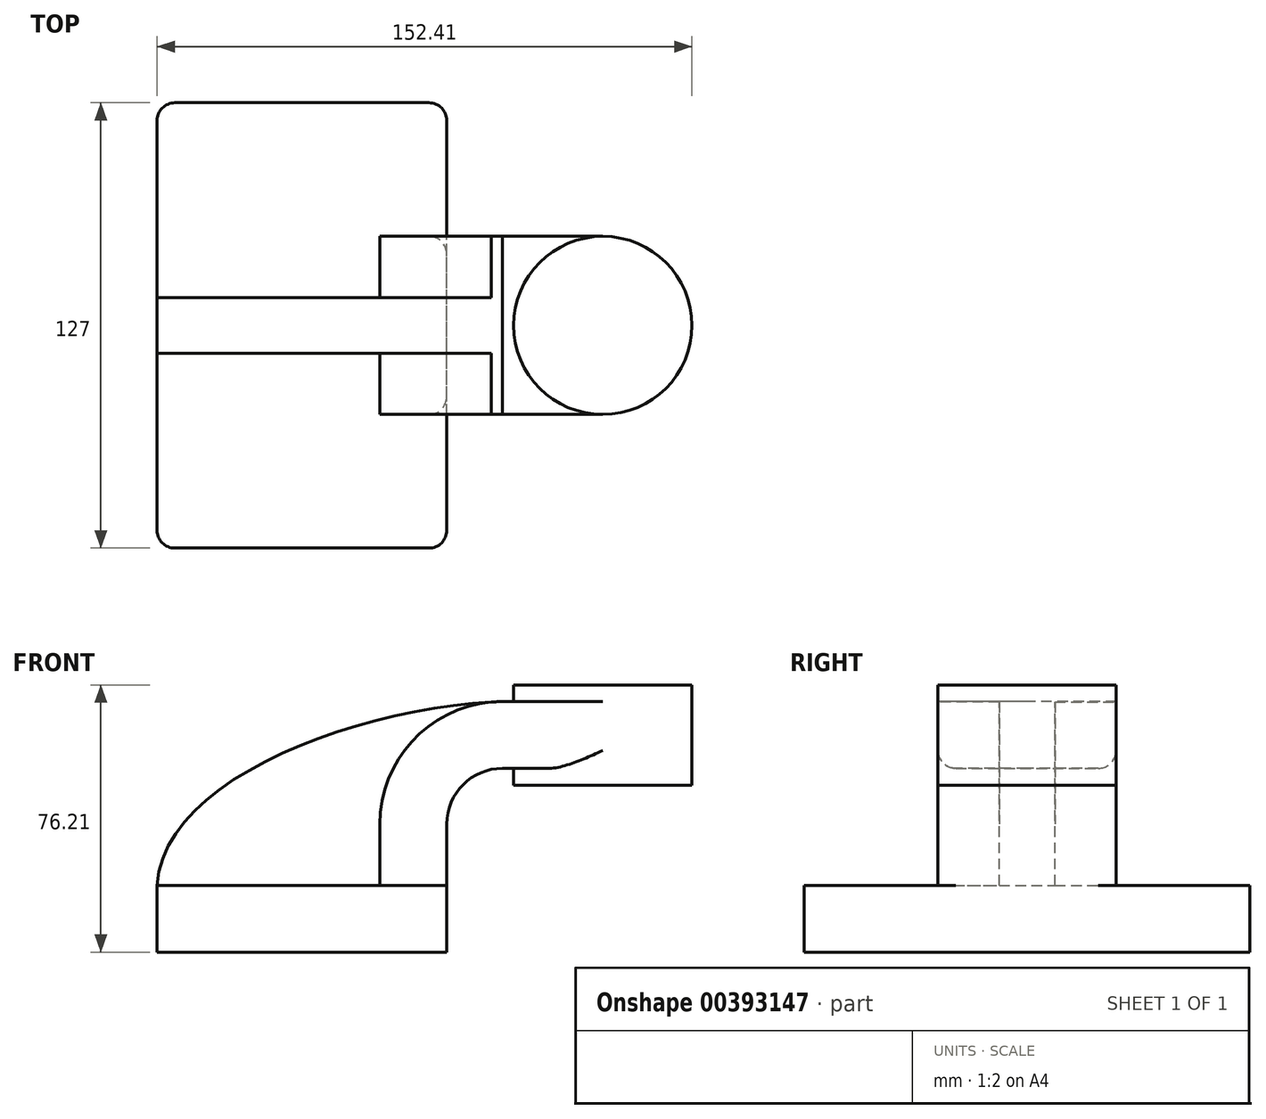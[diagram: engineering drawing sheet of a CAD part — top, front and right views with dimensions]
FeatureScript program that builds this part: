
annotation { "Feature Type Name" : "Feature", "Feature Type Description" : "" }
export const myFeature = defineFeature(function(context is Context, id is Id, definition is map)
    precondition{}
    {
        {
            var Q0;
            Q0=qCreatedBy(makeId("Front.planeOp"),FACE);
            var sketch = newSketch(context, id + "F0", { "sketchPlane" : qUnion([Q0])});
            skLineSegment(sketch, "E0.rect.bottom", {"start": v(-41.28, 9.52) * mm, "end": v(41.28, 9.52) * mm});
            skLineSegment(sketch, "E0.rect.top", {"start": v(-41.28, -9.52) * mm, "end": v(41.28, -9.52) * mm});
            skLineSegment(sketch, "E0.rect.left", {"start": v(-41.28, 9.52) * mm, "end": v(-41.28, -9.52) * mm});
            skLineSegment(sketch, "E0.rect.right", {"start": v(41.28, 9.52) * mm, "end": v(41.28, -9.52) * mm});
            skPoint(sketch, "E0.rect.middle", {"position": v(0, 0) * mm});
            skLineSegment(sketch, "E1", {"start": v(41.28, 9.52) * mm, "end": v(41.28, 27) * mm});
            skArc(sketch, "E2", {"start": v(41.28, 27) * mm, "mid": v(45.92, 38.23) * mm, "end": v(57.15, 42.88) * mm});
            skLineSegment(sketch, "E3", {"start": v(57.15, 42.88) * mm, "end": v(85.72, 42.88) * mm});
            skLineSegment(sketch, "E4.rect.bottom", {"start": v(60.32, 38.1) * mm, "end": v(111.12, 38.1) * mm});
            skLineSegment(sketch, "E4.rect.top", {"start": v(60.32, 66.68) * mm, "end": v(111.12, 66.68) * mm});
            skLineSegment(sketch, "E4.rect.left", {"start": v(60.32, 38.1) * mm, "end": v(60.32, 66.68) * mm});
            skLineSegment(sketch, "E4.rect.right", {"start": v(111.13, 38.1) * mm, "end": v(111.12, 66.68) * mm});
            skPoint(sketch, "E4.rect.middle", {"position": v(85.72, 52.39) * mm});
            skLineSegment(sketch, "E5.0", {"start": v(57.15, 61.93) * mm, "end": v(85.72, 61.93) * mm});
            skArc(sketch, "E5.1", {"start": v(22.23, 27) * mm, "mid": v(32.45, 51.7) * mm, "end": v(57.15, 61.93) * mm});
            skLineSegment(sketch, "E5.2", {"start": v(22.23, 9.52) * mm, "end": v(22.23, 27) * mm});
            skLineSegment(sketch, "E6", {"start": v(85.72, 38.1) * mm, "end": v(85.72, 66.68) * mm});
            skFitSpline(sketch, "E7", {"points": [v(-41.28, 9.53) * mm, v(57.15, 61.93) * mm], "startDerivative": vector(5.2, 92.34) * mm, "endDerivative": vector(120.92, 4.22) * mm});
            skSolve(sketch);
        }
        {
            var Q0;
            {var subQ4=sQuery(id+"F0.wireOp",EDGE,"E1");Q0=makeQuery(id+"F0.imprint","IMPRINT",FACE,{"disambiguationData":[TD([[makeQuery(id+"F0.imprint","IMPRINT",EDGE,{"derivedFrom":subQ4}),1.0]])]});}
            var Q1;
            {var subQ0=sQuery(id+"F0.wireOp",EDGE,"E6");var subQ1=sQuery(id+"F0.wireOp",EDGE,"E3");var subQ2=makeQuery(id+"F0.imprint","INTERSECT",VERTEX,{"derivedFrom":[subQ1,subQ0]});Q1=makeQuery(id+"F0.imprint","IMPRINT",FACE,{"disambiguationData":[TD([[makeQuery(id+"F0.imprint","IMPRINT",EDGE,{"disambiguationData":[TD([[subQ2,1.0]])],"derivedFrom":subQ1}),1.0]])]});}
            extrude(context, id + "F1", {"entities" : qUnion([Q0, Q1]), "endBound" : BoundingType.SYMMETRIC, "depth" : 12.7 * mm});
        }
        {
            var Q0;
            {var subQ0=sQuery(id+"F0.wireOp",EDGE,"E4.rect.right");Q0=makeQuery(id+"F0.imprint","IMPRINT",FACE,{"disambiguationData":[TD([[makeQuery(id+"F0.imprint","IMPRINT",EDGE,{"derivedFrom":subQ0}),1.0]])]});}
            var Q1;
            Q1=sQuery(id+"F0.wireOp",EDGE,"E6");
            revolve(context, id + "F2", {"operationType" : NewBodyOperationType.ADD, "entities" : qUnion([Q0]), "axis" : qUnion([Q1]), "revolveType" : RevolveType.FULL});
        }
        {
            var Q0;
            Q0=makeQuery(id+"F0.imprint","IMPRINT",FACE,{"disambiguationData":[TD([[makeQuery(id+"F0.imprint","IMPRINT",EDGE,{"derivedFrom":sQuery(id+"F0.wireOp",EDGE,"E0.rect.top")}),1.0]])]});
            extrude(context, id + "F3", {"entities" : qUnion([Q0]), "endBound" : BoundingType.SYMMETRIC, "depth" : 127 * mm});
        }
        {
            var Q0;
            {var subQ9=sQuery(id+"F0.wireOp",EDGE,"E1");Q0=makeQuery(id+"F0.imprint","IMPRINT",FACE,{"disambiguationData":[TD([[makeQuery(id+"F0.imprint","IMPRINT",EDGE,{"derivedFrom":subQ9}),1.0]])]});}
            var Q1;
            {var subQ0=sQuery(id+"F0.wireOp",EDGE,"E6");var subQ1=sQuery(id+"F0.wireOp",EDGE,"E3");var subQ2=makeQuery(id+"F0.imprint","INTERSECT",VERTEX,{"derivedFrom":[subQ1,subQ0]});Q1=makeQuery(id+"F0.imprint","IMPRINT",FACE,{"disambiguationData":[TD([[makeQuery(id+"F0.imprint","IMPRINT",EDGE,{"disambiguationData":[TD([[subQ2,1.0]])],"derivedFrom":subQ1}),1.0]])]});}
            extrude(context, id + "F4", {"entities" : qUnion([Q0, Q1]), "operationType" : NewBodyOperationType.ADD, "endBound" : BoundingType.SYMMETRIC, "depth" : 50.8 * mm});
        }
        {
            var Q0;
            {var subQ3=sQuery(id+"F0.wireOp",EDGE,"E5.2");Q0=makeQuery(id+"F0.imprint","IMPRINT",FACE,{"disambiguationData":[TD([[makeQuery(id+"F0.imprint","IMPRINT",EDGE,{"derivedFrom":subQ3}),1.0]])]});}
            extrude(context, id + "F5", {"entities" : qUnion([Q0]), "operationType" : NewBodyOperationType.ADD, "endBound" : BoundingType.SYMMETRIC, "depth" : 15.88 * mm});
        }
        {
            var Q0;
            {var subQ5=sQuery(id+"F0.wireOp",EDGE,"E4.rect.right");Q0=makeQuery(id+"F0.imprint","IMPRINT",FACE,{"disambiguationData":[TD([[makeQuery(id+"F0.imprint","IMPRINT",EDGE,{"derivedFrom":subQ5}),1.0]])]});}
            var Q1;
            Q1=sQuery(id+"F0.wireOp",EDGE,"E6");
            revolve(context, id + "F6", {"operationType" : NewBodyOperationType.ADD, "entities" : qUnion([Q0]), "axis" : qUnion([Q1]), "revolveType" : RevolveType.FULL});
        }
        {
            var Q0;
            Q0=makeQuery(id+"F3.opExtrude","CAP_EDGE",EDGE,{"disambiguationData":[OSD([sQuery(id+"F0.wireOp",EDGE,"E0.rect.right")])],"isStart":false});
            var Q1;
            Q1=makeQuery(id+"F3.opExtrude","CAP_EDGE",EDGE,{"disambiguationData":[OSD([sQuery(id+"F0.wireOp",EDGE,"E0.rect.left")])],"isStart":false});
            var Q2;
            Q2=makeQuery(id+"F3.opExtrude","CAP_EDGE",EDGE,{"disambiguationData":[OSD([sQuery(id+"F0.wireOp",EDGE,"E0.rect.right")])],"isStart":true});
            var Q3;
            Q3=makeQuery(id+"F3.opExtrude","CAP_EDGE",EDGE,{"disambiguationData":[OSD([sQuery(id+"F0.wireOp",EDGE,"E0.rect.left")])],"isStart":true});
            fillet(context, id + "F7", {"entities" : qUnion([Q0, Q1, Q2, Q3]), "radius" : 5.08 * mm, "tangentPropagation" : true, "allowEdgeOverflow" : false});
        }
        {
            var Q0;
            Q0=makeQuery(id+"F4.opExtrude","CAP_EDGE",EDGE,{"disambiguationData":[OSD([sQuery(id+"F0.wireOp",EDGE,"E2")])],"isStart":false});
            var Q1;
            Q1=makeQuery(id+"F4.opExtrude","CAP_EDGE",EDGE,{"disambiguationData":[OSD([sQuery(id+"F0.wireOp",EDGE,"E2")])],"isStart":true});
            fillet(context, id + "F8", {"entities" : qUnion([Q0, Q1]), "radius" : 5.08 * mm, "tangentPropagation" : true, "allowEdgeOverflow" : false});
        }
    });
